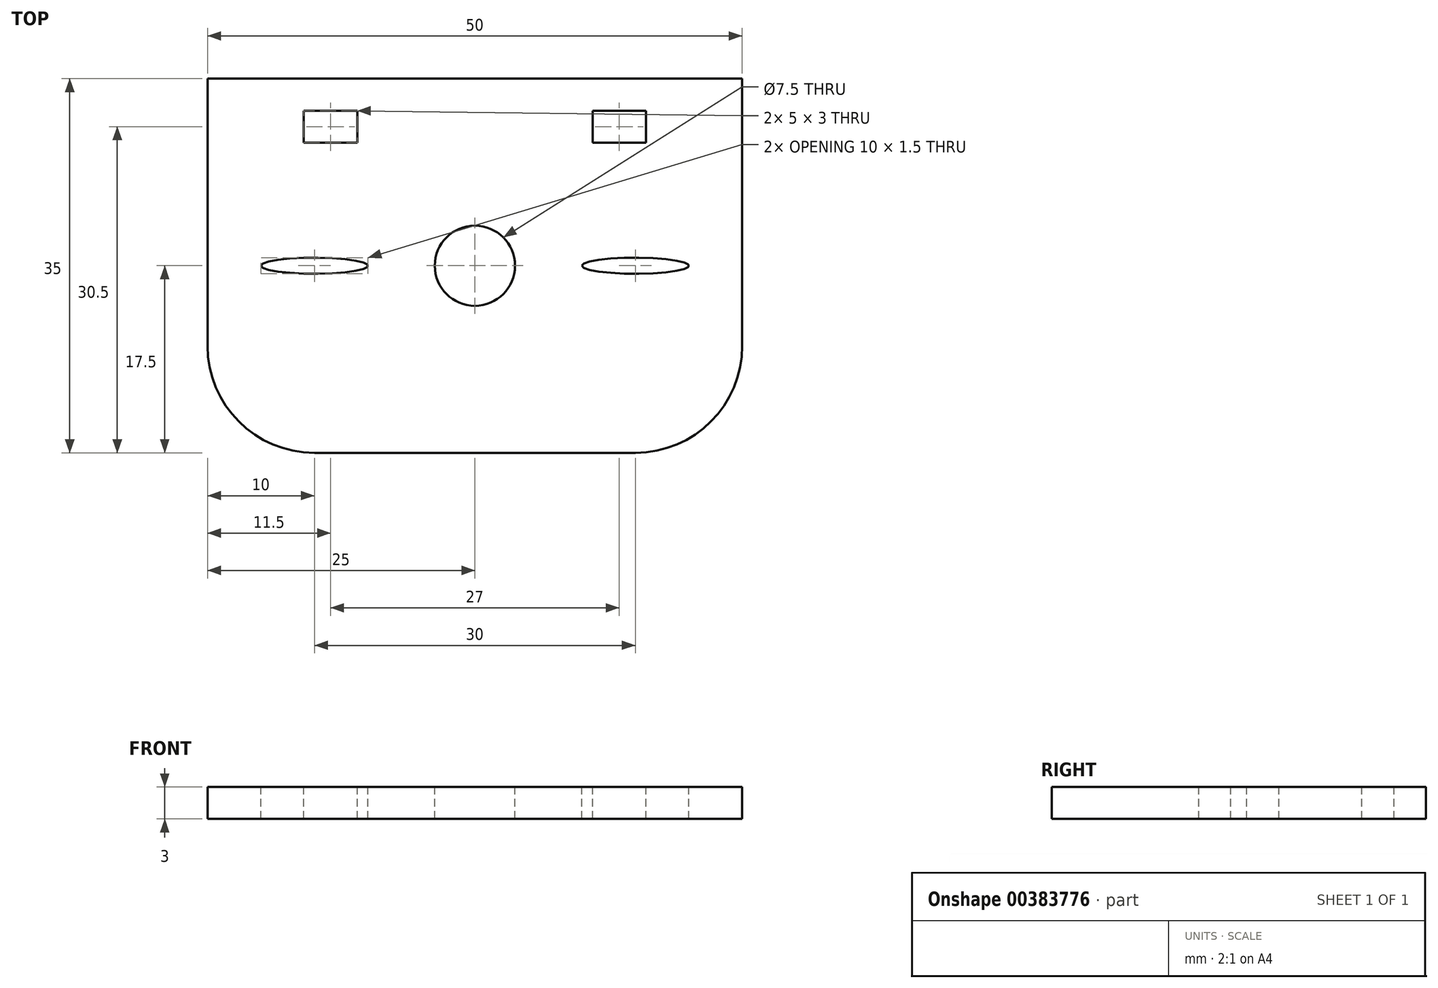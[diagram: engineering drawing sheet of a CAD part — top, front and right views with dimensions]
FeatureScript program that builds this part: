
annotation { "Feature Type Name" : "Feature", "Feature Type Description" : "" }
export const myFeature = defineFeature(function(context is Context, id is Id, definition is map)
    precondition{}
    {
        {
            var Q0;
            Q0=qCreatedBy(makeId("Top.planeOp"),FACE);
            var sketch = newSketch(context, id + "F0", { "sketchPlane" : qUnion([Q0])});
            skLineSegment(sketch, "E0.bottom", {"start": v(-25, 17.5) * mm, "end": v(25, 17.5) * mm});
            skLineSegment(sketch, "E0.top", {"start": v(-15, -17.5) * mm, "end": v(15, -17.5) * mm});
            skLineSegment(sketch, "E0.left", {"start": v(-25, 17.5) * mm, "end": v(-25, -7.5) * mm});
            skLineSegment(sketch, "E0.right", {"start": v(25, 17.5) * mm, "end": v(25, -7.5) * mm});
            skPoint(sketch, "E0.middle", {"position": v(0, 0) * mm});
            skCircle(sketch, "E1", {"center": v(0, 0) * mm, "radius": 3.75 * mm});
            skLineSegment(sketch, "E2.bottom", {"start": v(-16, 14.5) * mm, "end": v(-11, 14.5) * mm});
            skLineSegment(sketch, "E2.top", {"start": v(-16, 11.5) * mm, "end": v(-11, 11.5) * mm});
            skLineSegment(sketch, "E2.left", {"start": v(-16, 14.5) * mm, "end": v(-16, 11.5) * mm});
            skLineSegment(sketch, "E2.right", {"start": v(-11, 14.5) * mm, "end": v(-11, 11.5) * mm});
            skPoint(sketch, "E2.middle", {"position": v(-13.5, 13) * mm});
            skLineSegment(sketch, "E3", {"start": v(-25, 17.5) * mm, "end": v(-25, 14.5) * mm, "construction": true});
            skLineSegment(sketch, "E4", {"start": v(-25, 14.5) * mm, "end": v(25, 14.5) * mm, "construction": true});
            skLineSegment(sketch, "E5", {"start": v(-25, 14.5) * mm, "end": v(-16, 14.5) * mm, "construction": true});
            skPoint(sketch, "E5.endSnap0", {"position": v(0, 14.5) * mm});
            skLineSegment(sketch, "E6", {"start": v(-16, 14.5) * mm, "end": v(-16, 17.5) * mm, "construction": true});
            skLineSegment(sketch, "E7.bottom", {"start": v(11, 14.5) * mm, "end": v(16, 14.5) * mm});
            skLineSegment(sketch, "E7.top", {"start": v(11, 11.5) * mm, "end": v(16, 11.5) * mm});
            skLineSegment(sketch, "E7.left", {"start": v(11, 14.5) * mm, "end": v(11, 11.5) * mm});
            skLineSegment(sketch, "E7.right", {"start": v(16, 14.5) * mm, "end": v(16, 11.5) * mm});
            skPoint(sketch, "E7.middle", {"position": v(13.5, 13) * mm});
            skLineSegment(sketch, "E8", {"start": v(16, 14.5) * mm, "end": v(16, 17.5) * mm, "construction": true});
            skLineSegment(sketch, "E9", {"start": v(16, 14.5) * mm, "end": v(25, 14.5) * mm, "construction": true});
            skEllipse(sketch, "E10", {"center": v(-15, 0) * mm, "majorRadius": 5 * mm, "minorRadius": 0.75 * mm, "majorAxis": v(-1, 0)});
            skEllipse(sketch, "E11", {"center": v(15, 0) * mm, "majorRadius": 5 * mm, "minorRadius": 0.75 * mm, "majorAxis": v(-1, 0)});
            skLineSegment(sketch, "E12", {"start": v(-15, 0) * mm, "end": v(0, 0) * mm, "construction": true});
            skLineSegment(sketch, "E13", {"start": v(0, 0) * mm, "end": v(15, 0) * mm, "construction": true});
            skPoint(sketch, "E14.visualSharp", {"position": v(25, -17.5) * mm});
            skArc(sketch, "E14.filletArc", {"start": v(15, -17.5) * mm, "mid": v(22.07, -14.57) * mm, "end": v(25, -7.5) * mm});
            skPoint(sketch, "E15.visualSharp", {"position": v(-25, -17.5) * mm});
            skArc(sketch, "E15.filletArc", {"start": v(-25, -7.5) * mm, "mid": v(-22.07, -14.57) * mm, "end": v(-15, -17.5) * mm});
            skSolve(sketch);
        }
        {
            var Q0;
            Q0=makeQuery(id+"F0.imprint","IMPRINT",FACE,{"disambiguationData":[TD([[makeQuery(id+"F0.imprint","IMPRINT",EDGE,{"derivedFrom":sQuery(id+"F0.wireOp",EDGE,"E0.bottom")}),-1.0]])]});
            extrude(context, id + "F1", {"entities" : qUnion([Q0]), "oppositeDirection" : true, "depth" : 3 * mm});
        }
    });
